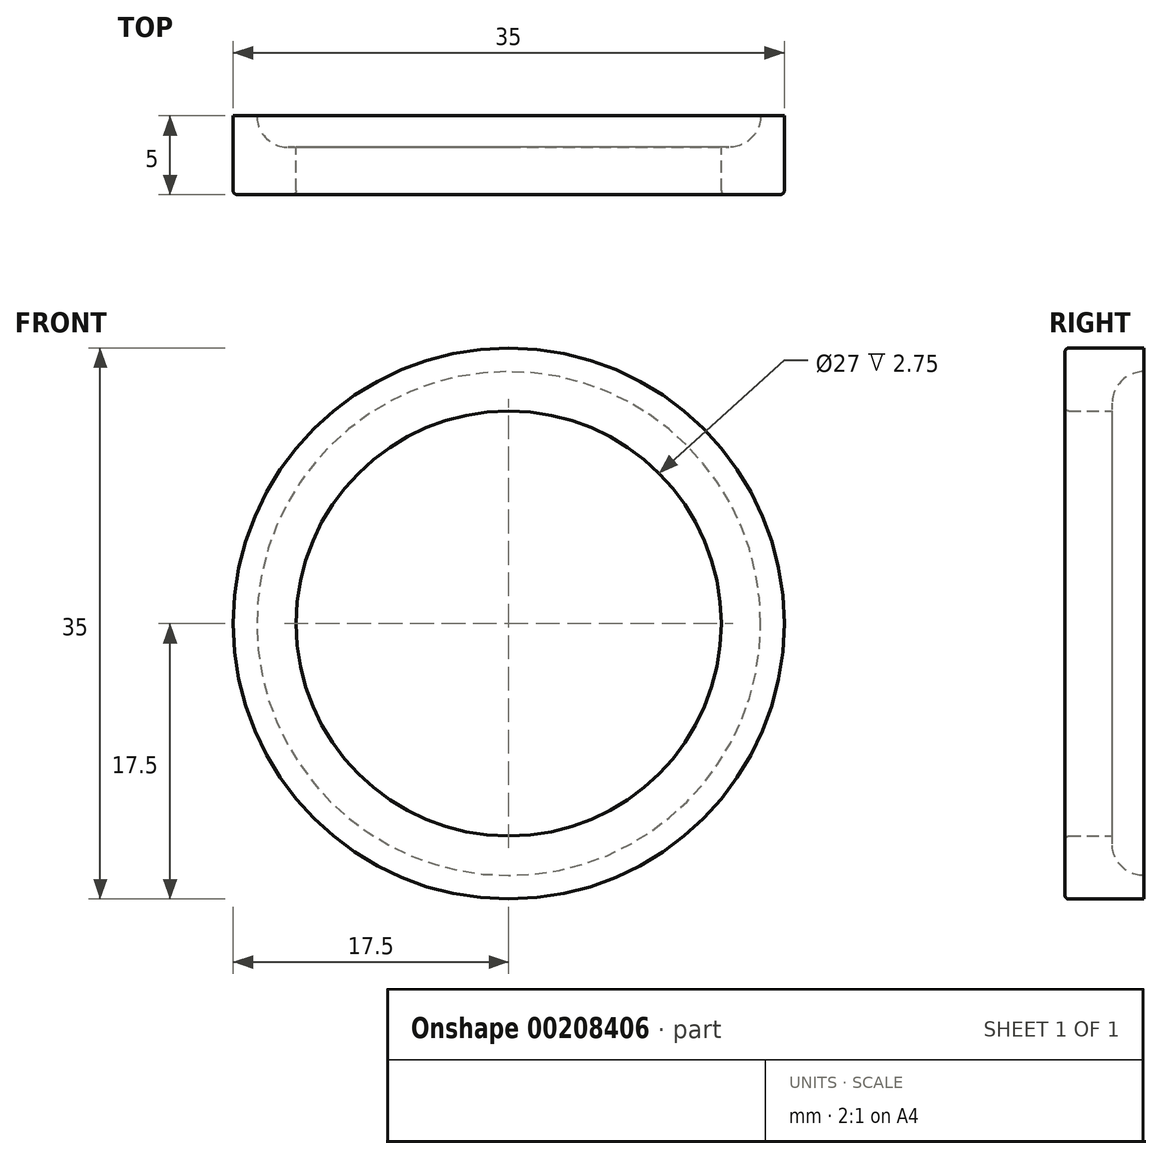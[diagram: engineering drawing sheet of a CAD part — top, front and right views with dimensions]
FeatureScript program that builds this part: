
annotation { "Feature Type Name" : "Feature", "Feature Type Description" : "" }
export const myFeature = defineFeature(function(context is Context, id is Id, definition is map)
    precondition{}
    {
        {
            var Q0;
            Q0=qCreatedBy(makeId("Front.planeOp"),FACE);
            var sketch = newSketch(context, id + "F0", { "sketchPlane" : qUnion([Q0])});
            skCircle(sketch, "E0", {"center": v(0, 0) * mm, "radius": 13.5 * mm});
            skCircle(sketch, "E1", {"center": v(0, 0) * mm, "radius": 17.5 * mm});
            skSolve(sketch);
        }
        {
            var Q0;
            Q0 = qSketchRegion(id + "F0", true);
            extrude(context, id + "F1", {"entities" : qUnion([Q0]), "depth" : 5 * mm});
        }
        {
            var Q0;
            Q0=makeQuery(id+"F1.opExtrude","CAP_EDGE",EDGE,{"disambiguationData":[OSD([sQuery(id+"F0.wireOp",EDGE,"E1")])],"isStart":false});
            var Q1;
            Q1=makeQuery(id+"F1.opExtrude","CAP_EDGE",EDGE,{"disambiguationData":[OSD([sQuery(id+"F0.wireOp",EDGE,"E0")])],"isStart":false});
            fillet(context, id + "F2", {"entities" : qUnion([Q0, Q1]), "radius" : 0.25 * mm, "tangentPropagation" : true, "allowEdgeOverflow" : false});
        }
        {
            var Q0;
            Q0=qCreatedBy(makeId("Front.planeOp"),FACE);
            var sketch = newSketch(context, id + "F3", { "sketchPlane" : qUnion([Q0])});
            skCircle(sketch, "E2", {"center": v(0, 0) * mm, "radius": 16 * mm});
            skSolve(sketch);
        }
        {
            var Q0;
            Q0=makeQuery(id+"F3.imprint","IMPRINT",FACE,{"disambiguationData":[TD([[makeQuery(id+"F3.imprint","IMPRINT",EDGE,{"derivedFrom":sQuery(id+"F3.wireOp",EDGE,"E2")}),1.0]])]});
            extrude(context, id + "F4", {"entities" : qUnion([Q0]), "operationType" : NewBodyOperationType.REMOVE, "depth" : 2 * mm});
        }
        {
            var Q0;
            Q0=makeQuery(id+"F4.boolean.opBoolean","COPY",EDGE,{"derivedFrom":makeQuery(id+"F4.opExtrude","CAP_EDGE",EDGE,{"disambiguationData":[OSD([sQuery(id+"F3.wireOp",EDGE,"E2")])],"isStart":false})});
            fillet(context, id + "F5", {"entities" : qUnion([Q0]), "radius" : 2 * mm, "tangentPropagation" : true, "allowEdgeOverflow" : false});
        }
    });
